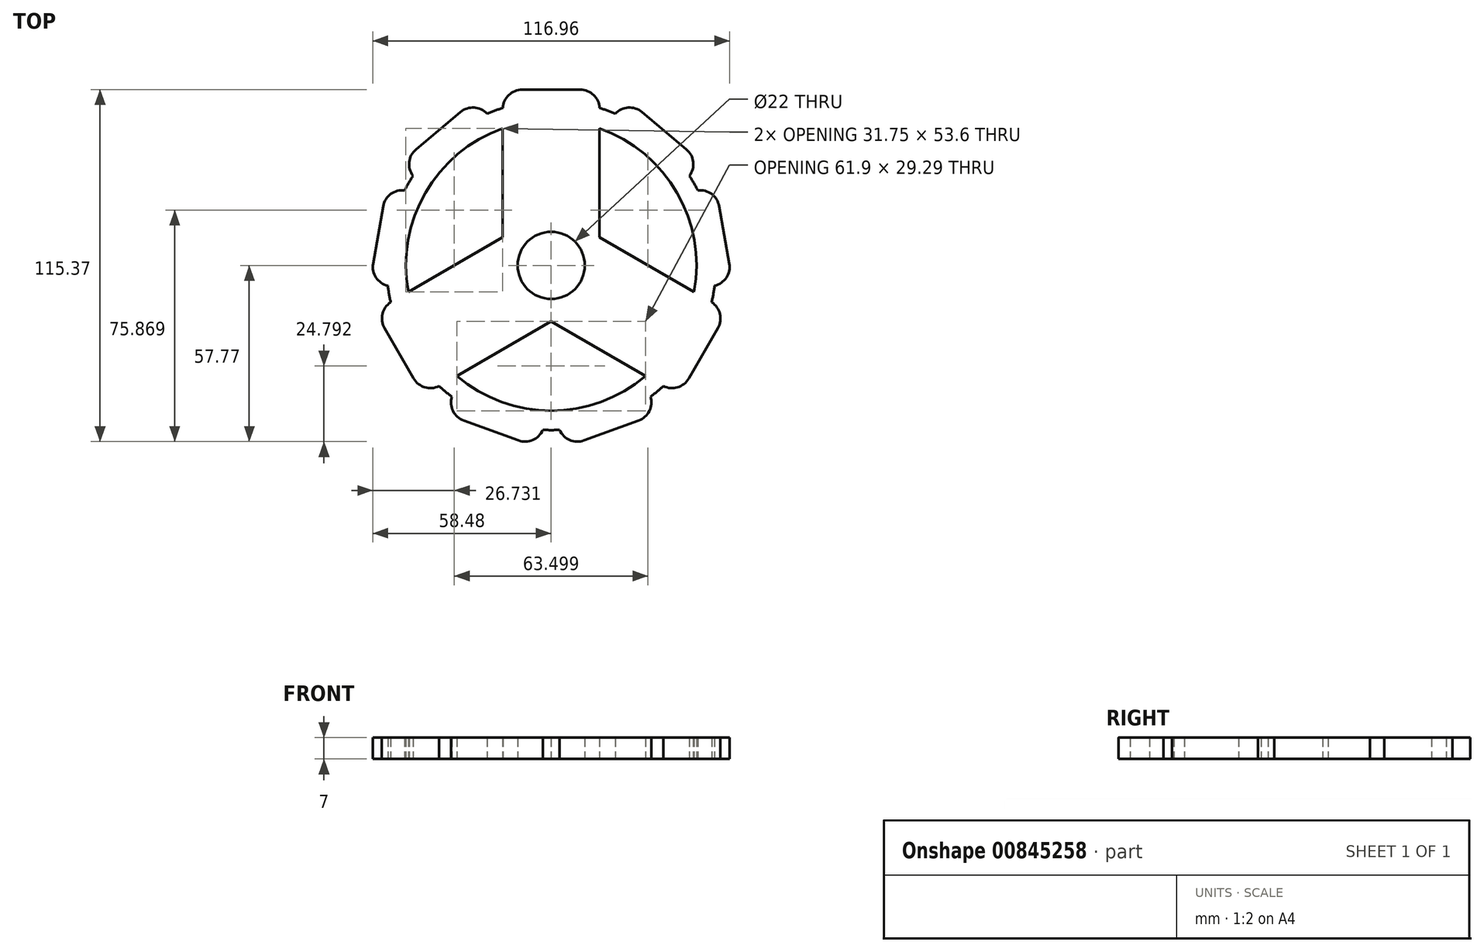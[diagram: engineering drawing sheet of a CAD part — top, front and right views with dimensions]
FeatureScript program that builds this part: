
annotation { "Feature Type Name" : "Feature", "Feature Type Description" : "" }
export const myFeature = defineFeature(function(context is Context, id is Id, definition is map)
    precondition{}
    {
        {
            var Q0;
            Q0=qCreatedBy(makeId("Top.planeOp"),FACE);
            var sketch = newSketch(context, id + "F0", { "sketchPlane" : qUnion([Q0])});
            skCircle(sketch, "E0", {"center": v(0, 0) * mm, "radius": 11 * mm});
            skCircle(sketch, "E1", {"center": v(0, 0) * mm, "radius": 15.88 * mm});
            skCircle(sketch, "E2", {"center": v(0, 0) * mm, "radius": 47.63 * mm});
            skCircle(sketch, "E3", {"center": v(0, 0) * mm, "radius": 53.98 * mm});
            skLineSegment(sketch, "E4.left", {"start": v(-15.88, 9.17) * mm, "end": v(-15.88, 44.9) * mm});
            skLineSegment(sketch, "E4.right", {"start": v(15.87, 9.17) * mm, "end": v(15.87, 44.9) * mm});
            skPoint(sketch, "E5.orphan", {"position": v(-15.88, 0) * mm});
            skPoint(sketch, "E6.orphan", {"position": v(-7.94, 13.75) * mm});
            skPoint(sketch, "E7.orphan", {"position": v(7.94, 13.75) * mm});
            skPoint(sketch, "E8.orphan", {"position": v(15.88, 0) * mm});
            skPoint(sketch, "E9.orphan", {"position": v(7.94, -13.75) * mm});
            skPoint(sketch, "E10.orphan", {"position": v(-7.94, -13.75) * mm});
            skLineSegment(sketch, "E11", {"start": v(-15.88, 0) * mm, "end": v(-15.88, 9.17) * mm, "construction": true});
            skLineSegment(sketch, "E12", {"start": v(15.88, 0) * mm, "end": v(15.88, 9.17) * mm, "construction": true});
            skLineSegment(sketch, "E13.1.0", {"start": v(0, -18.33) * mm, "end": v(-30.95, -36.2) * mm});
            skLineSegment(sketch, "E13.1.1", {"start": v(7.94, -13.75) * mm, "end": v(0, -18.33) * mm, "construction": true});
            skLineSegment(sketch, "E13.1.2", {"start": v(-15.87, 9.17) * mm, "end": v(-46.82, -8.7) * mm});
            skLineSegment(sketch, "E13.1.3", {"start": v(-7.94, 13.75) * mm, "end": v(-15.87, 9.17) * mm, "construction": true});
            skLineSegment(sketch, "E13.2.0", {"start": v(15.88, 9.17) * mm, "end": v(46.82, -8.7) * mm});
            skLineSegment(sketch, "E13.2.1", {"start": v(7.94, 13.75) * mm, "end": v(15.88, 9.17) * mm, "construction": true});
            skLineSegment(sketch, "E13.2.2", {"start": v(0, -18.33) * mm, "end": v(30.95, -36.2) * mm});
            skLineSegment(sketch, "E13.2.3", {"start": v(-7.94, -13.75) * mm, "end": v(0, -18.33) * mm, "construction": true});
            skLineSegment(sketch, "E14.bottom", {"start": v(-15.88, 44.9) * mm, "end": v(15.87, 44.9) * mm});
            skLineSegment(sketch, "E14.top", {"start": v(-9.53, 57.6) * mm, "end": v(9.52, 57.6) * mm});
            skLineSegment(sketch, "E14.left", {"start": v(-15.88, 44.9) * mm, "end": v(-15.88, 51.25) * mm});
            skLineSegment(sketch, "E14.right", {"start": v(15.87, 44.9) * mm, "end": v(15.87, 51.25) * mm});
            skPoint(sketch, "E15.visualSharp", {"position": v(15.88, 57.6) * mm});
            skArc(sketch, "E15.filletArc", {"start": v(15.87, 51.25) * mm, "mid": v(14.02, 55.74) * mm, "end": v(9.52, 57.6) * mm});
            skPoint(sketch, "E16.visualSharp", {"position": v(-15.88, 57.6) * mm});
            skArc(sketch, "E16.filletArc", {"start": v(-9.53, 57.6) * mm, "mid": v(-14.02, 55.74) * mm, "end": v(-15.88, 51.25) * mm});
            skLineSegment(sketch, "E17.1.0", {"start": v(-41.02, 24.2) * mm, "end": v(-45.1, 29.06) * mm});
            skLineSegment(sketch, "E17.1.1", {"start": v(-41.02, 24.2) * mm, "end": v(-16.7, 44.6) * mm});
            skLineSegment(sketch, "E17.1.2", {"start": v(-16.7, 44.6) * mm, "end": v(-20.78, 49.47) * mm});
            skArc(sketch, "E17.1.3", {"start": v(-44.32, 38) * mm, "mid": v(-46.57, 33.7) * mm, "end": v(-45.1, 29.06) * mm});
            skLineSegment(sketch, "E17.1.4", {"start": v(-44.32, 38) * mm, "end": v(-29.73, 50.25) * mm});
            skArc(sketch, "E17.1.5", {"start": v(-20.78, 49.47) * mm, "mid": v(-25.1, 51.7) * mm, "end": v(-29.73, 50.25) * mm});
            skLineSegment(sketch, "E17.2.0", {"start": v(-46.98, -7.84) * mm, "end": v(-53.23, -6.73) * mm});
            skLineSegment(sketch, "E17.2.1", {"start": v(-46.98, -7.84) * mm, "end": v(-41.46, 23.43) * mm});
            skLineSegment(sketch, "E17.2.2", {"start": v(-41.46, 23.43) * mm, "end": v(-47.72, 24.53) * mm});
            skArc(sketch, "E17.2.3", {"start": v(-58.38, 0.62) * mm, "mid": v(-57.33, -4.12) * mm, "end": v(-53.23, -6.73) * mm});
            skLineSegment(sketch, "E17.2.4", {"start": v(-58.38, 0.62) * mm, "end": v(-55.07, 19.38) * mm});
            skArc(sketch, "E17.2.5", {"start": v(-47.72, 24.53) * mm, "mid": v(-52.46, 23.48) * mm, "end": v(-55.07, 19.38) * mm});
            skLineSegment(sketch, "E17.3.0", {"start": v(-30.95, -36.2) * mm, "end": v(-36.45, -39.37) * mm});
            skLineSegment(sketch, "E17.3.1", {"start": v(-30.95, -36.2) * mm, "end": v(-46.82, -8.7) * mm});
            skLineSegment(sketch, "E17.3.2", {"start": v(-46.82, -8.7) * mm, "end": v(-52.32, -11.88) * mm});
            skArc(sketch, "E17.3.3", {"start": v(-45.12, -37.05) * mm, "mid": v(-41.27, -40) * mm, "end": v(-36.45, -39.37) * mm});
            skLineSegment(sketch, "E17.3.4", {"start": v(-45.12, -37.05) * mm, "end": v(-54.65, -20.55) * mm});
            skArc(sketch, "E17.3.5", {"start": v(-52.32, -11.88) * mm, "mid": v(-55.28, -15.73) * mm, "end": v(-54.65, -20.55) * mm});
            skLineSegment(sketch, "E17.4.0", {"start": v(-0.44, -47.62) * mm, "end": v(-2.61, -53.6) * mm});
            skLineSegment(sketch, "E17.4.1", {"start": v(-0.44, -47.62) * mm, "end": v(-30.27, -36.76) * mm});
            skLineSegment(sketch, "E17.4.2", {"start": v(-30.27, -36.76) * mm, "end": v(-32.45, -42.73) * mm});
            skArc(sketch, "E17.4.3", {"start": v(-10.75, -57.39) * mm, "mid": v(-5.9, -57.17) * mm, "end": v(-2.61, -53.6) * mm});
            skLineSegment(sketch, "E17.4.4", {"start": v(-10.75, -57.39) * mm, "end": v(-28.65, -50.87) * mm});
            skArc(sketch, "E17.4.5", {"start": v(-32.45, -42.73) * mm, "mid": v(-32.23, -47.59) * mm, "end": v(-28.65, -50.87) * mm});
            skLineSegment(sketch, "E17.5.0", {"start": v(30.27, -36.76) * mm, "end": v(32.45, -42.73) * mm});
            skLineSegment(sketch, "E17.5.1", {"start": v(30.27, -36.76) * mm, "end": v(0.44, -47.62) * mm});
            skLineSegment(sketch, "E17.5.2", {"start": v(0.44, -47.62) * mm, "end": v(2.61, -53.6) * mm});
            skArc(sketch, "E17.5.3", {"start": v(28.65, -50.87) * mm, "mid": v(32.23, -47.59) * mm, "end": v(32.45, -42.73) * mm});
            skLineSegment(sketch, "E17.5.4", {"start": v(28.65, -50.87) * mm, "end": v(10.75, -57.39) * mm});
            skArc(sketch, "E17.5.5", {"start": v(2.61, -53.6) * mm, "mid": v(5.9, -57.17) * mm, "end": v(10.75, -57.39) * mm});
            skLineSegment(sketch, "E17.6.0", {"start": v(46.82, -8.7) * mm, "end": v(52.32, -11.88) * mm});
            skLineSegment(sketch, "E17.6.1", {"start": v(46.82, -8.7) * mm, "end": v(30.95, -36.2) * mm});
            skLineSegment(sketch, "E17.6.2", {"start": v(30.95, -36.2) * mm, "end": v(36.45, -39.37) * mm});
            skArc(sketch, "E17.6.3", {"start": v(54.65, -20.55) * mm, "mid": v(55.28, -15.73) * mm, "end": v(52.32, -11.88) * mm});
            skLineSegment(sketch, "E17.6.4", {"start": v(54.65, -20.55) * mm, "end": v(45.12, -37.05) * mm});
            skArc(sketch, "E17.6.5", {"start": v(36.45, -39.37) * mm, "mid": v(41.27, -40) * mm, "end": v(45.12, -37.05) * mm});
            skLineSegment(sketch, "E17.7.0", {"start": v(41.46, 23.43) * mm, "end": v(47.72, 24.53) * mm});
            skLineSegment(sketch, "E17.7.1", {"start": v(41.46, 23.43) * mm, "end": v(46.98, -7.84) * mm});
            skLineSegment(sketch, "E17.7.2", {"start": v(46.98, -7.84) * mm, "end": v(53.23, -6.73) * mm});
            skArc(sketch, "E17.7.3", {"start": v(55.07, 19.38) * mm, "mid": v(52.46, 23.48) * mm, "end": v(47.72, 24.53) * mm});
            skLineSegment(sketch, "E17.7.4", {"start": v(55.07, 19.38) * mm, "end": v(58.38, 0.62) * mm});
            skArc(sketch, "E17.7.5", {"start": v(53.23, -6.73) * mm, "mid": v(57.33, -4.12) * mm, "end": v(58.38, 0.62) * mm});
            skLineSegment(sketch, "E17.8.0", {"start": v(16.7, 44.6) * mm, "end": v(20.78, 49.47) * mm});
            skLineSegment(sketch, "E17.8.1", {"start": v(16.7, 44.6) * mm, "end": v(41.02, 24.2) * mm});
            skLineSegment(sketch, "E17.8.2", {"start": v(41.02, 24.2) * mm, "end": v(45.1, 29.06) * mm});
            skArc(sketch, "E17.8.3", {"start": v(29.73, 50.25) * mm, "mid": v(25.1, 51.7) * mm, "end": v(20.78, 49.47) * mm});
            skLineSegment(sketch, "E17.8.4", {"start": v(29.73, 50.25) * mm, "end": v(44.32, 38) * mm});
            skArc(sketch, "E17.8.5", {"start": v(45.1, 29.06) * mm, "mid": v(46.57, 33.7) * mm, "end": v(44.32, 38) * mm});
            skSolve(sketch);
        }
        {
            var Q0;
            Q0 = qSketchRegion(id + "F0", true);
            var Q1;
            Q1=makeQuery(id+"F0.imprint","IMPRINT",FACE,{"disambiguationData":[TD([[makeQuery(id+"F0.imprint","IMPRINT",EDGE,{"derivedFrom":sQuery(id+"F0.wireOp",EDGE,"E1")}),-1.0]])]});
            var Q2;
            Q2=makeQuery(id+"F0.imprint","IMPRINT",FACE,{"disambiguationData":[TD([[makeQuery(id+"F0.imprint","IMPRINT",EDGE,{"derivedFrom":sQuery(id+"F0.wireOp",EDGE,"E0")}),-1.0]])]});
            var Q3;
            {var subQ0=sQuery(id+"F0.wireOp",EDGE,"E14.bottom");Q3=makeQuery(id+"F0.imprint","IMPRINT",FACE,{"disambiguationData":[TD([[makeQuery(id+"F0.imprint","IMPRINT",EDGE,{"derivedFrom":subQ0}),1.0]])]});}
            var Q4;
            {var subQ0=sQuery(id+"F0.wireOp",EDGE,"E17.3.1");Q4=makeQuery(id+"F0.imprint","IMPRINT",FACE,{"disambiguationData":[TD([[makeQuery(id+"F0.imprint","IMPRINT",EDGE,{"derivedFrom":subQ0}),1.0]])]});}
            var Q5;
            {var subQ0=sQuery(id+"F0.wireOp",EDGE,"E17.6.1");Q5=makeQuery(id+"F0.imprint","IMPRINT",FACE,{"disambiguationData":[TD([[makeQuery(id+"F0.imprint","IMPRINT",EDGE,{"derivedFrom":subQ0}),1.0]])]});}
            extrude(context, id + "F1", {"entities" : qUnion([Q0, Q1, Q2, Q3, Q4, Q5]), "depth" : 7 * mm, "offsetDistance" : 25.4 * mm});
        }
    });
